# Revit family: Atdec - MonitorMounts_AWMS_2_4640-1
name_source: partatom
category: Specialty Equipment
revit_build: Autodesk Revit 2014 (Build: 20130308_1515(x64)
units: mm (PartAtom-declared; Revit-internal decimal feet)

## types (1)
- AWMS-2-4640
    Arm = ATD - Aluminum Silver
    Assembly Code = E1010800
    Bilt-in arm rotation limiter = Yes
    Colour Options = Silver, Black, White
    Cost = 0 $
    Cover = ATD - Aluminum Silver
    Default Elevation = 0 mm  [stored 0 ft]
    Description = Atdec modular dual monitor mount (Load: 0-12kg/ 26lb per arm)
    Height Adjustable = Yes
    Landscape to Portrait Rotation = Yes
    Manufacturer = Atdec
    Material = Aluminium, composite plastic
    Model = AWMS-2-4640
    Mounting Hole Pattern = 75x75, 100x100
    Mounting Options Included = No
    Note = Choose your preferred desk fixing option
    Option = Bolt though (AWM-FB), C type desk clamp (AWM-FC), F type desk clamp (AWM-FF), Heavy duty desk clamp (AWM-FH), Grommet mount (AC-GC)
    Optional  Post Height = 750mm (29.5")
    Post = ATD - Aluminum Silver
    Post Height = 400mm (15.7")
    Product Family = Modular monitor mounts
    Spring-Assisted = No
    Support Plate = ATD - Aluminum Black
    Supported Weight Range = 0-12kg
    URL = www.atdec.com.au
    Upgradable to Support Additional Arm(s) = Yes
    Warranty = 10 Years

note: [stored X ft] marks values corroborated as IEEE doubles in the binary element streams (Revit-internal decimal feet)

## geometry (parser evidence)
native form markers: Sweep x2
no freeform markers — native parametric forms only
